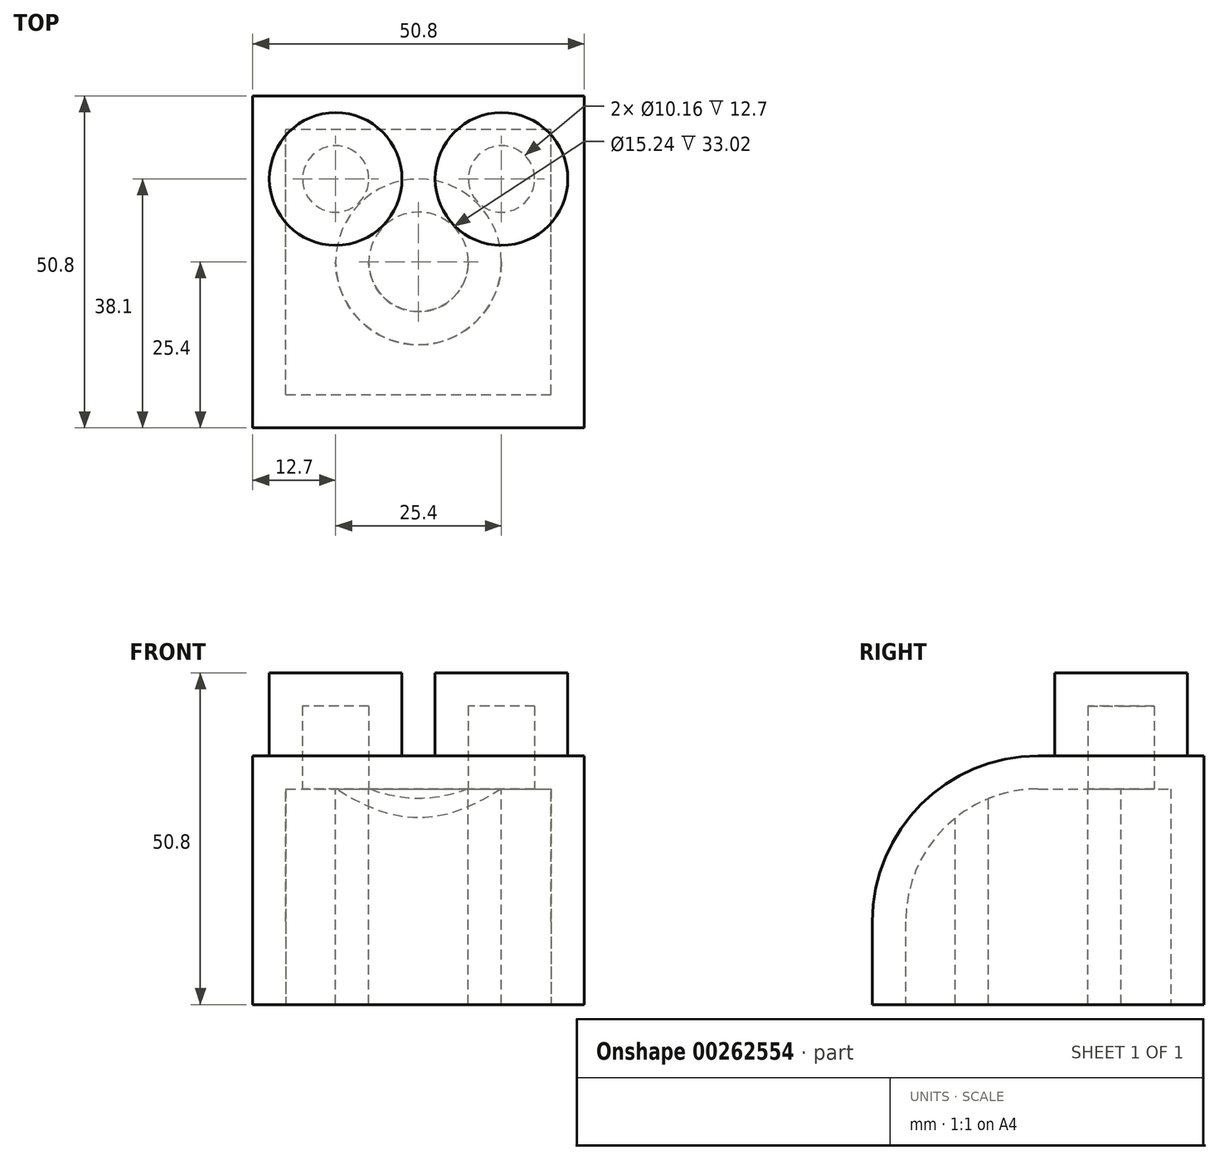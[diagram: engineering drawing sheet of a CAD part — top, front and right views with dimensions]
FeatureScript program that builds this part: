
annotation { "Feature Type Name" : "Feature", "Feature Type Description" : "" }
export const myFeature = defineFeature(function(context is Context, id is Id, definition is map)
    precondition{}
    {
        {
            var Q0;
            Q0=qCreatedBy(makeId("Top.planeOp"),FACE);
            var sketch = newSketch(context, id + "F0", { "sketchPlane" : qUnion([Q0])});
            skLineSegment(sketch, "E0.bottom", {"start": v(0, 0) * mm, "end": v(50.8, 0) * mm});
            skLineSegment(sketch, "E0.top", {"start": v(0, 50.8) * mm, "end": v(50.8, 50.8) * mm});
            skLineSegment(sketch, "E0.left", {"start": v(0, 0) * mm, "end": v(0, 50.8) * mm});
            skLineSegment(sketch, "E0.right", {"start": v(50.8, 0) * mm, "end": v(50.8, 50.8) * mm});
            skSolve(sketch);
        }
        {
            var Q0;
            Q0=makeQuery(id+"F0.imprint","IMPRINT",FACE,{"disambiguationData":[TD([[makeQuery(id+"F0.imprint","IMPRINT",EDGE,{"derivedFrom":sQuery(id+"F0.wireOp",EDGE,"E0.bottom")}),1.0]])]});
            extrude(context, id + "F1", {"entities" : qUnion([Q0]), "depth" : 38.1 * mm});
        }
        {
            var Q0;
            Q0=makeQuery(id+"F1.opExtrude","CAP_EDGE",EDGE,{"disambiguationData":[OSD([sQuery(id+"F0.wireOp",EDGE,"E0.bottom")])],"isStart":false});
            fillet(context, id + "F2", {"entities" : qUnion([Q0]), "radius" : 25.4 * mm, "tangentPropagation" : true, "allowEdgeOverflow" : false});
        }
        {
            var Q0;
            Q0=makeQuery(id+"F1.opExtrude","CAP_FACE",FACE,{"disambiguationData":[OSD([sQuery(id+"F0.wireOp",EDGE,"E0.bottom"),sQuery(id+"F0.wireOp",EDGE,"E0.top"),sQuery(id+"F0.wireOp",EDGE,"E0.left"),sQuery(id+"F0.wireOp",EDGE,"E0.right")])],"isStart":false});
            var sketch = newSketch(context, id + "F3", { "sketchPlane" : qUnion([Q0])});
            skPoint(sketch, "E1.centerSnap0", {"position": v(0, 38.1) * mm});
            skCircle(sketch, "E2", {"center": v(12.7, 38.1) * mm, "radius": 10.16 * mm});
            skCircle(sketch, "E3", {"center": v(38.1, 38.1) * mm, "radius": 10.16 * mm});
            skPoint(sketch, "E3.centerSnap0", {"position": v(50.8, 38.1) * mm});
            skSolve(sketch);
        }
        {
            var Q0;
            Q0=makeQuery(id+"F3.imprint","IMPRINT",FACE,{"disambiguationData":[TD([[makeQuery(id+"F3.imprint","IMPRINT",EDGE,{"derivedFrom":sQuery(id+"F3.wireOp",EDGE,"E2")}),1.0]])]});
            var Q1;
            Q1=makeQuery(id+"F3.imprint","IMPRINT",FACE,{"disambiguationData":[TD([[makeQuery(id+"F3.imprint","IMPRINT",EDGE,{"derivedFrom":sQuery(id+"F3.wireOp",EDGE,"E3")}),1.0]])]});
            extrude(context, id + "F4", {"entities" : qUnion([Q0, Q1]), "operationType" : NewBodyOperationType.ADD, "depth" : 12.7 * mm});
        }
        {
            var Q0;
            Q0=makeQuery(id+"F1.opExtrude","CAP_FACE",FACE,{"disambiguationData":[OSD([sQuery(id+"F0.wireOp",EDGE,"E0.bottom"),sQuery(id+"F0.wireOp",EDGE,"E0.top"),sQuery(id+"F0.wireOp",EDGE,"E0.left"),sQuery(id+"F0.wireOp",EDGE,"E0.right")])],"isStart":true});
            shell(context, id + "F5", {"entities" : qUnion([Q0]), "thickness" : 5.08 * mm});
        }
        {
            var Q0;
            Q0=makeQuery(id+"F5.opShell","OFFSET_FACE",FACE,{"disambiguationData":[OSD([sQuery(id+"F0.wireOp",EDGE,"E0.bottom"),sQuery(id+"F0.wireOp",EDGE,"E0.top"),sQuery(id+"F0.wireOp",EDGE,"E0.left"),sQuery(id+"F0.wireOp",EDGE,"E0.right")])]});
            var sketch = newSketch(context, id + "F6", { "sketchPlane" : qUnion([Q0])});
            skCircle(sketch, "E4", {"center": v(25.4, -25.4) * mm, "radius": 12.7 * mm});
            skSolve(sketch);
        }
        {
            var Q0;
            {var subQ0=sQuery(id+"F6.wireOp",EDGE,"E4");var subQ1=makeQuery(id+"F5.opShell","OFFSET_EDGE",EDGE,{"disambiguationData":[OSD([sQuery(id+"F0.wireOp",EDGE,"E0.bottom"),sQuery(id+"F0.wireOp",EDGE,"E0.top"),sQuery(id+"F0.wireOp",EDGE,"E0.left"),sQuery(id+"F0.wireOp",EDGE,"E0.right")])]});var subQ2=makeQuery(id+"F6.imprint","INTERSECT",VERTEX,{"disambiguationData":[OD(0.0)],"derivedFrom":[subQ1,subQ0]});Q0=makeQuery(id+"F6.imprint","IMPRINT",FACE,{"disambiguationData":[TD([[makeQuery(id+"F6.imprint","IMPRINT",EDGE,{"disambiguationData":[TD([[subQ2,1.0]])],"derivedFrom":subQ0}),1.0]])]});}
            var Q1;
            {var subQ0=sQuery(id+"F6.wireOp",EDGE,"E4");var subQ1=makeQuery(id+"F5.opShell","OFFSET_EDGE",EDGE,{"disambiguationData":[OSD([sQuery(id+"F0.wireOp",EDGE,"E0.bottom"),sQuery(id+"F0.wireOp",EDGE,"E0.top"),sQuery(id+"F0.wireOp",EDGE,"E0.left"),sQuery(id+"F0.wireOp",EDGE,"E0.right")])]});var subQ2=makeQuery(id+"F6.imprint","INTERSECT",VERTEX,{"disambiguationData":[OD(0.0)],"derivedFrom":[subQ1,subQ0]});Q1=makeQuery(id+"F6.imprint","IMPRINT",FACE,{"disambiguationData":[TD([[makeQuery(id+"F6.imprint","IMPRINT",EDGE,{"disambiguationData":[TD([[subQ2,-1.0]])],"derivedFrom":subQ0}),1.0]])]});}
            extrude(context, id + "F7", {"entities" : qUnion([Q0, Q1]), "operationType" : NewBodyOperationType.ADD, "depth" : 33.02 * mm});
        }
        {
            var Q0;
            Q0=makeQuery(id+"F7.opExtrude","CAP_FACE",FACE,{"disambiguationData":[OSD([sQuery(id+"F6.wireOp",EDGE,"E4")])],"isStart":false});
            shell(context, id + "F8", {"entities" : qUnion([Q0]), "thickness" : 5.08 * mm});
        }
    });
